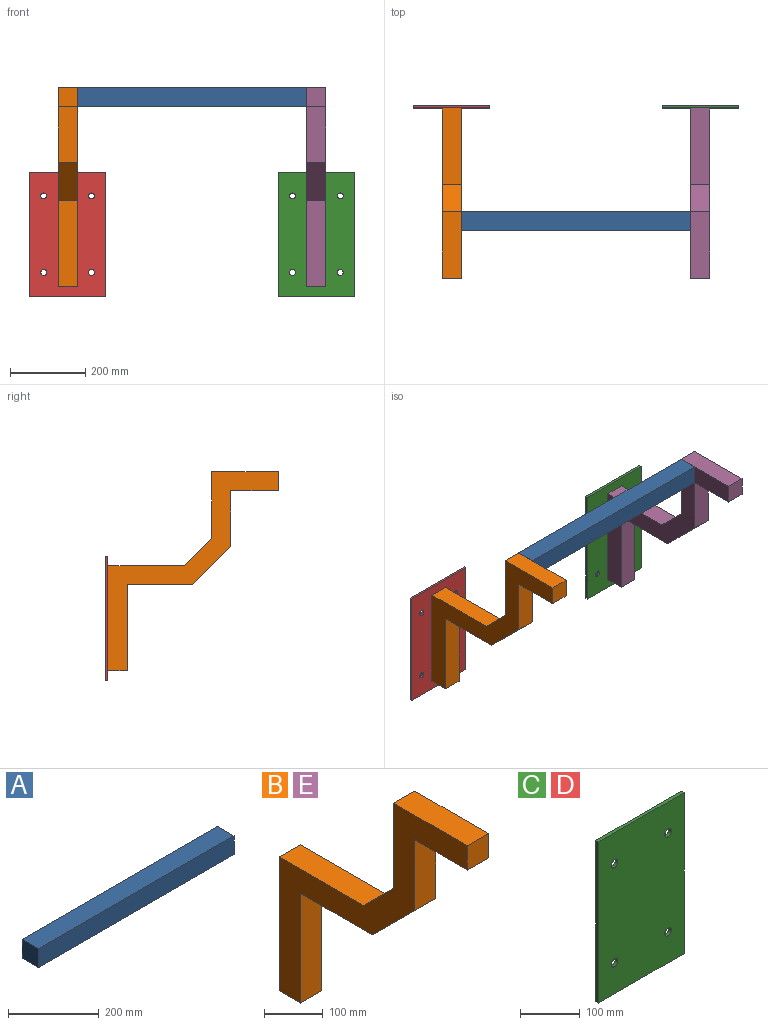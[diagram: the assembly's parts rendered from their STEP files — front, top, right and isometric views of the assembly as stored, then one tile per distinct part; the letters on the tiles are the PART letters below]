
ASSEMBLY  parts=5 mates=4
PART A: 6 faces, bbox 609.6x50.8x50.8 mm
  f0: plane 609.6x50.8mm, normal (0,-1,0), area 30967.7mm2, adj f1,f3,f4,f5
  f1: plane 609.6x50.8mm, normal (0,0,-1), area 30967.7mm2, adj f0,f2,f4,f5
  f2: plane 609.6x50.8mm, normal (0,1,0), area 30967.7mm2, adj f1,f3,f4,f5
  f3: plane 609.6x50.8mm, normal (0,0,1), area 30967.7mm2, adj f0,f2,f4,f5
  f4: plane 50.8x50.8mm, normal (1,0,0), area 2580.6mm2, adj f0,f1,f2,f3
  f5: plane 50.8x50.8mm, normal (-1,0,0), area 2580.6mm2, adj f0,f1,f2,f3
PART B: 14 faces, bbox 50.8x452.8x529 mm
  f0: plane 177.8x50.8mm, normal (0,0,1), area 9032.2mm2, adj f1,f11,f12,f13
  f1: plane 50.8x50.8mm, normal (0,-1,0), area 2580.6mm2, adj f0,f2,f12,f13
  f2: plane 127x50.8mm, normal (0,0,-1), area 6451.6mm2, adj f1,f3,f12,f13
  f3: plane 148.04x50.8mm, normal (0,-1,0), area 7520.5mm2, adj f2,f4,f12,f13
  f4: plane 101.6x101.6mm, normal (0,-0.71,-0.71), area 7299.2mm2, adj f3,f5,f12,f13
  f5: plane 173.44x50.8mm, normal (0,0,-1), area 8810.9mm2, adj f4,f6,f12,f13
  f6: plane 228.6x50.8mm, normal (0,-1,0), area 11612.9mm2, adj f5,f7,f12,f13
  f7: plane 50.8x50.8mm, normal (0,0,-1), area 2580.6mm2, adj f6,f8,f12,f13
  f8: plane 279.4x50.8mm, normal (0,1,0), area 14193.5mm2, adj f7,f9,f12,f13
  f9: plane 203.2x50.8mm, normal (0,0,1), area 10322.6mm2, adj f8,f10,f12,f13
  f10: plane 71.84x71.84mm, normal (0,0.71,0.71), area 5161.3mm2, adj f9,f11,f12,f13
  f11: plane 177.8x50.8mm, normal (0,1,0), area 9032.2mm2, adj f0,f10,f12,f13
  f12: plane 529.04x452.84mm, normal (1,0,0), area 44718.4mm2, adj f0,f1,f2,f3,f4,f5,f6,f7
  f13: plane 529.04x452.84mm, normal (-1,0,0), area 44718.4mm2, adj f0,f1,f2,f3,f4,f5,f6,f7
PART C: 10 faces, bbox 203.2x6.4x330.2 mm
  f0: cylinder r=7.94mm len=15.88mm, axis (0,-1,0), area 316.7mm2, adj f7,f8
  f1: cylinder r=7.94mm len=15.88mm, axis (0,-1,0), area 316.7mm2, adj f7,f8
  f2: cylinder r=7.94mm len=15.88mm, axis (0,-1,0), area 316.7mm2, adj f7,f8
  f3: plane 203.2x6.35mm, normal (0,0,1), area 1290.3mm2, adj f4,f6,f7,f8
  f4: plane 330.2x6.35mm, normal (-1,0,0), area 2096.8mm2, adj f3,f5,f7,f8
  f5: plane 203.2x6.35mm, normal (0,0,-1), area 1290.3mm2, adj f4,f6,f7,f8
  f6: plane 330.2x6.35mm, normal (1,0,0), area 2096.8mm2, adj f3,f5,f7,f8
  f7: plane 330.2x203.2mm, normal (0,-1,0), area 66304.9mm2, adj f0,f1,f2,f3,f4,f5,f6,f9
  f8: plane 330.2x203.2mm, normal (0,1,0), area 66304.9mm2, adj f0,f1,f2,f3,f4,f5,f6,f9
  f9: cylinder r=7.94mm len=15.88mm, axis (0,-1,0), area 316.7mm2, adj f7,f8
PART D: same geometry as C
PART E: same geometry as B
PLACE A t=(-161.02,37.52,-55.53)mm
PLACE B t=(-211.82,-89.48,-4.73)mm
PLACE C t=(372.38,369.71,-228.98)mm
PLACE D t=(-288.02,369.71,-228.98)mm
PLACE E t=(448.58,-89.48,-4.73)mm
MATE fastened B.f0 <-> A.f3  axis (0,0,1) through (-161.02,88.32,-4.73)mm
MATE fastened E.f0 <-> A.f3  axis (0,0,1) through (448.58,88.32,-4.73)mm
MATE fastened D.f7 <-> B.f8  axis (0,-1,0) through (-186.42,363.36,-394.08)mm
MATE fastened C.f7 <-> E.f8  axis (0,-1,0) through (473.98,363.36,-394.08)mm
